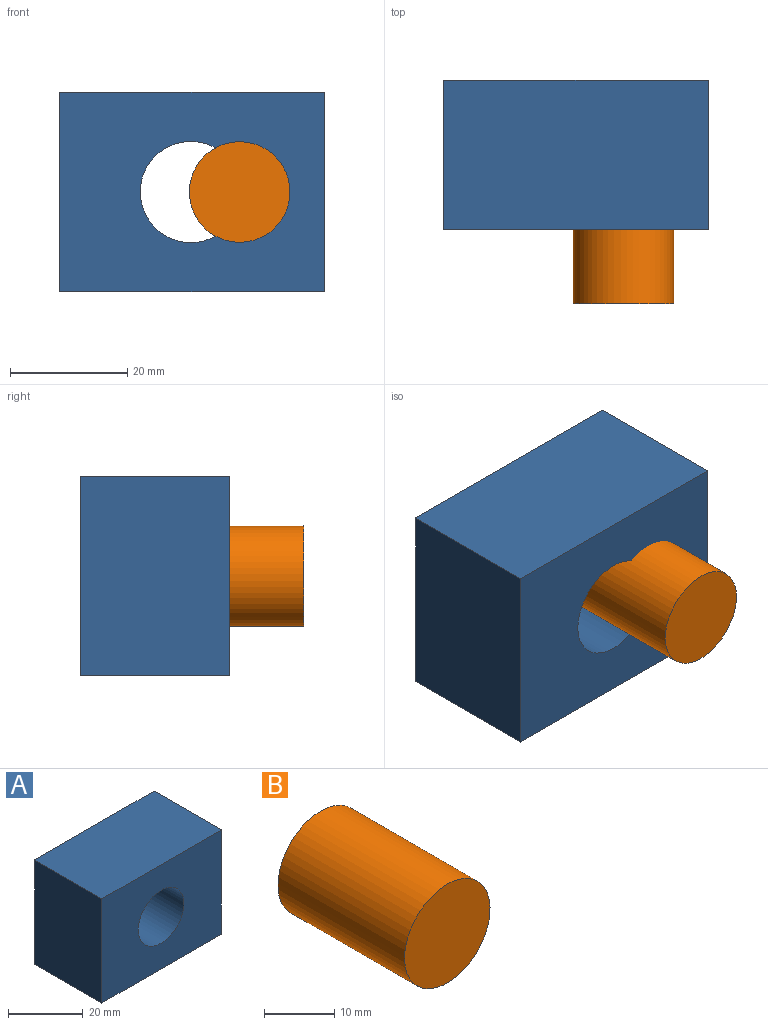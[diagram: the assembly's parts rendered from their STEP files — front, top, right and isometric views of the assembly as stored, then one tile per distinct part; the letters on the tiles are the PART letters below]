
ASSEMBLY  parts=2 mates=1
PART A: 7 faces, bbox 45.1x25.4x34.1 mm
  f0: plane 34.06x25.4mm, normal (-1,0,0), area 865.1mm2, adj f1,f3,f5,f6
  f1: plane 45.07x25.4mm, normal (0,0,-1), area 1144.8mm2, adj f0,f2,f5,f6
  f2: plane 34.06x25.4mm, normal (1,0,0), area 865.1mm2, adj f1,f3,f5,f6
  f3: plane 45.07x25.4mm, normal (0,0,1), area 1144.8mm2, adj f0,f2,f5,f6
  f4: cylinder r=8.62mm len=25.4mm, axis (0,1,0), area 1376.1mm2, adj f5,f6
  f5: plane 45.07x34.06mm, normal (0,-1,0), area 1301.5mm2, adj f0,f1,f2,f3,f4
  f6: plane 45.07x34.06mm, normal (0,1,0), area 1301.5mm2, adj f0,f1,f2,f3,f4
PART B: 3 faces, bbox 17.1x25.4x17.1 mm
  f0: cylinder r=8.57mm len=25.4mm, axis (0,1,0), area 1368.1mm2, adj f1,f2
  f1: plane 17.15x17.15mm, normal (0,-1,0), area 230.9mm2, adj f0
  f2: plane 17.15x17.15mm, normal (0,1,0), area 230.9mm2, adj f0
PLACE A t=(-52.84,7.03,-6.32)mm
PLACE B t=(-22.18,-5.67,10.71)mm
MATE pin_slot A.f4 <-> B.f0  axis (0,1,0) through (-30.51,-5.67,10.71)mm
